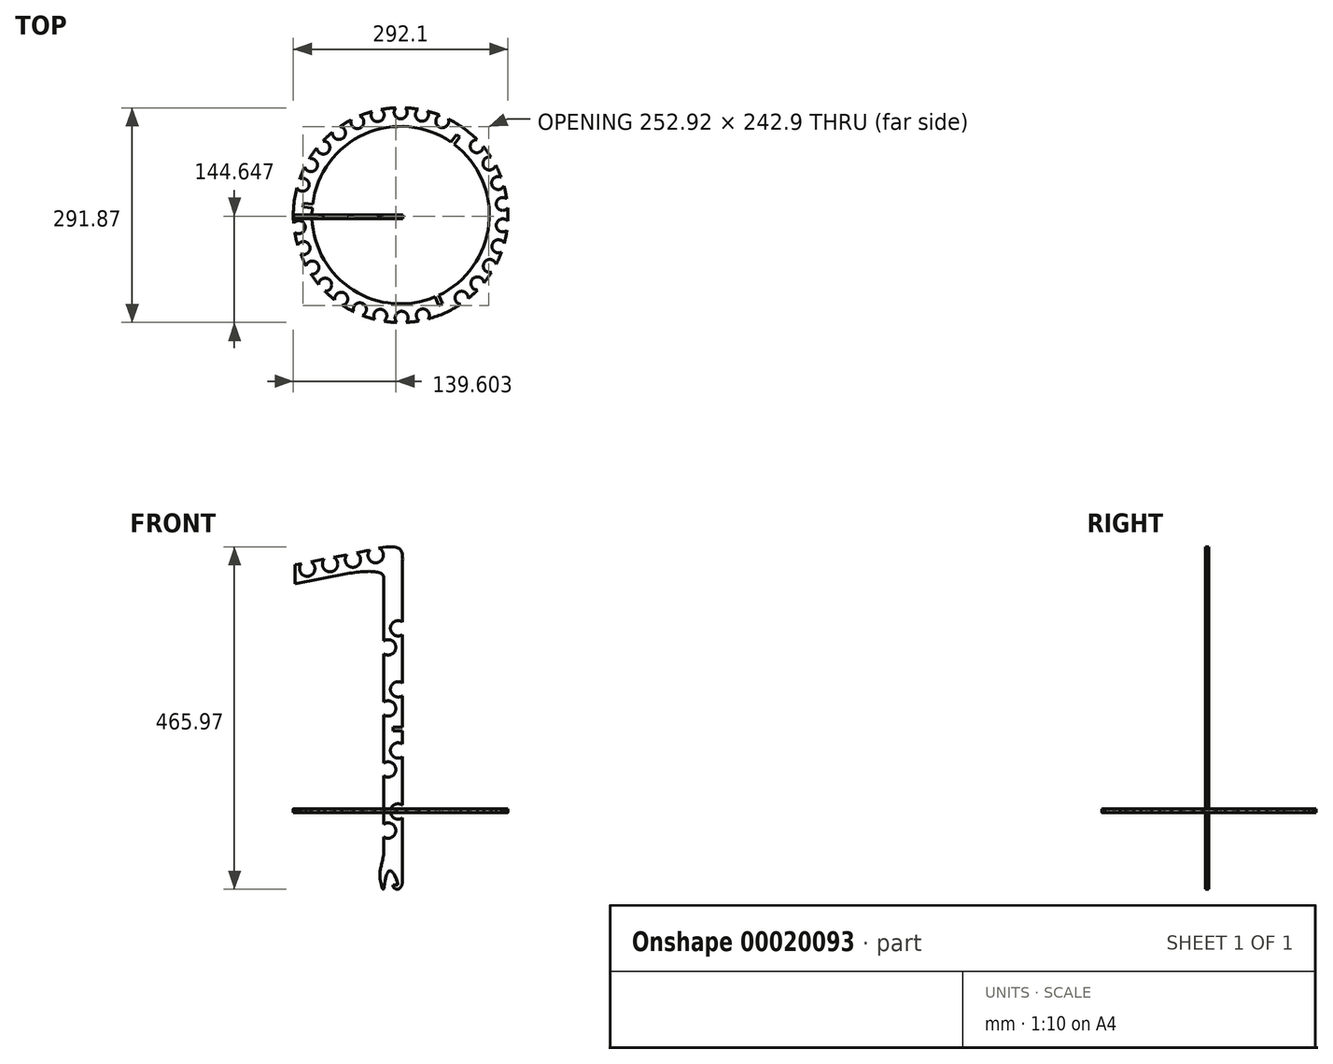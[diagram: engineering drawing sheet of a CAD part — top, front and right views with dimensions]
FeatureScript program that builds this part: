
annotation { "Feature Type Name" : "Feature", "Feature Type Description" : "" }
export const myFeature = defineFeature(function(context is Context, id is Id, definition is map)
    precondition{}
    {
        {
            var Q0;
            Q0=qCreatedBy(makeId("Top.planeOp"),FACE);
            var sketch = newSketch(context, id + "F0", { "sketchPlane" : qUnion([Q0])});
            skArc(sketch, "E0", {"start": v(-6.35, 145.91) * mm, "mid": v(-16.52, 145.11) * mm, "end": v(-26.62, 143.6) * mm});
            skArc(sketch, "E1", {"start": v(-120.25, 9.87) * mm, "mid": v(-70.74, -97.73) * mm, "end": v(46.94, -111.14) * mm});
            skArc(sketch, "E2", {"start": v(-6.35, 145.91) * mm, "mid": v(0, 130.8) * mm, "end": v(6.35, 145.91) * mm});
            skArc(sketch, "E3.1.0", {"start": v(24.04, 144.06) * mm, "mid": v(27.12, 127.96) * mm, "end": v(36.46, 141.42) * mm});
            skArc(sketch, "E3.2.0", {"start": v(53.38, 135.94) * mm, "mid": v(53.06, 119.56) * mm, "end": v(65, 130.8) * mm});
            skArc(sketch, "E3.4.0", {"start": v(103.94, 102.6) * mm, "mid": v(97, 87.75) * mm, "end": v(112.46, 93.18) * mm});
            skArc(sketch, "E3.5.0", {"start": v(122.95, 78.82) * mm, "mid": v(113.08, 65.74) * mm, "end": v(129.34, 67.84) * mm});
            skArc(sketch, "E3.6.0", {"start": v(136.62, 51.62) * mm, "mid": v(124.25, 40.86) * mm, "end": v(140.6, 39.55) * mm});
            skArc(sketch, "E3.7.0", {"start": v(144.36, 22.17) * mm, "mid": v(130.03, 14.22) * mm, "end": v(145.74, 9.55) * mm});
            skArc(sketch, "E3.8.0", {"start": v(145.82, -8.24) * mm, "mid": v(130.15, -13.05) * mm, "end": v(144.55, -20.88) * mm});
            skArc(sketch, "E3.9.0", {"start": v(140.94, -38.3) * mm, "mid": v(124.61, -39.75) * mm, "end": v(137.08, -50.4) * mm});
            skArc(sketch, "E3.10.0", {"start": v(129.94, -66.68) * mm, "mid": v(113.66, -64.72) * mm, "end": v(123.65, -77.72) * mm});
            skArc(sketch, "E3.11.0", {"start": v(113.3, -92.17) * mm, "mid": v(97.78, -86.88) * mm, "end": v(104.85, -101.67) * mm});
            skArc(sketch, "E3.12.0", {"start": v(91.72, -113.66) * mm, "mid": v(77.64, -105.27) * mm, "end": v(81.5, -121.2) * mm});
            skArc(sketch, "E3.14.0", {"start": v(37.73, -141.1) * mm, "mid": v(28.26, -127.71) * mm, "end": v(25.33, -143.84) * mm});
            skArc(sketch, "E3.15.0", {"start": v(7.66, -145.85) * mm, "mid": v(1.17, -130.8) * mm, "end": v(-5.04, -145.96) * mm});
            skArc(sketch, "E3.16.0", {"start": v(-22.75, -144.27) * mm, "mid": v(-25.97, -128.2) * mm, "end": v(-35.2, -141.75) * mm});
            skArc(sketch, "E3.17.0", {"start": v(-52.16, -136.42) * mm, "mid": v(-51.99, -120.03) * mm, "end": v(-63.82, -131.37) * mm});
            skArc(sketch, "E3.18.0", {"start": v(-79.31, -122.64) * mm, "mid": v(-75.74, -106.64) * mm, "end": v(-89.67, -115.28) * mm});
            skArc(sketch, "E3.19.0", {"start": v(-103.02, -103.53) * mm, "mid": v(-96.2, -88.62) * mm, "end": v(-111.62, -94.19) * mm});
            skArc(sketch, "E3.20.0", {"start": v(-122.24, -79.92) * mm, "mid": v(-112.49, -66.75) * mm, "end": v(-128.72, -69) * mm});
            skArc(sketch, "E3.21.0", {"start": v(-136.16, -52.84) * mm, "mid": v(-123.88, -41.98) * mm, "end": v(-140.23, -40.81) * mm});
            skArc(sketch, "E3.22.0", {"start": v(-144.15, -23.46) * mm, "mid": v(-129.9, -15.38) * mm, "end": v(-145.65, -10.85) * mm});
            skArc(sketch, "E3.24.0", {"start": v(-141.28, 37.03) * mm, "mid": v(-124.96, 38.63) * mm, "end": v(-137.53, 49.16) * mm});
            skArc(sketch, "E3.25.0", {"start": v(-130.53, 65.52) * mm, "mid": v(-114.24, 63.7) * mm, "end": v(-124.35, 76.6) * mm});
            skArc(sketch, "E3.26.0", {"start": v(-114.11, 91.15) * mm, "mid": v(-98.55, 86) * mm, "end": v(-105.76, 100.72) * mm});
            skArc(sketch, "E3.27.0", {"start": v(-92.73, 112.83) * mm, "mid": v(-78.58, 104.57) * mm, "end": v(-82.58, 120.46) * mm});
            skArc(sketch, "E3.28.0", {"start": v(-67.33, 129.6) * mm, "mid": v(-55.2, 118.59) * mm, "end": v(-55.81, 134.97) * mm});
            skArc(sketch, "E3.29.0", {"start": v(-39, 140.75) * mm, "mid": v(-29.4, 127.45) * mm, "end": v(-26.62, 143.6) * mm});
            skLineSegment(sketch, "E3.anchor1", {"start": v(0, 0) * mm, "end": v(-6.35, 145.91) * mm, "construction": true});
            skLineSegment(sketch, "E3.anchor2", {"start": v(0, 0) * mm, "end": v(-39, 140.75) * mm, "construction": true});
            skArc(sketch, "E4.trimOffspring", {"start": v(24.04, 144.06) * mm, "mid": v(15.22, 145.25) * mm, "end": v(6.35, 145.91) * mm});
            skLineSegment(sketch, "E5.bottom", {"start": v(76.13, 109.51) * mm, "end": v(80.25, 106.53) * mm});
            skLineSegment(sketch, "E5.left", {"start": v(68.67, 99.2) * mm, "end": v(76.13, 109.51) * mm});
            skLineSegment(sketch, "E5.right", {"start": v(72.78, 96.22) * mm, "end": v(80.25, 106.53) * mm});
            skLineSegment(sketch, "E6", {"start": v(0, 0) * mm, "end": v(81.9, 113.16) * mm, "construction": true});
            skPoint(sketch, "E7", {"position": v(65.28, 90.2) * mm});
            skPoint(sketch, "E8", {"position": v(78.19, 108.02) * mm});
            skLineSegment(sketch, "E9.1.0", {"start": v(-120.25, 9.87) * mm, "end": v(-132.9, 11.17) * mm});
            skLineSegment(sketch, "E9.1.1", {"start": v(-132.9, 11.17) * mm, "end": v(-132.38, 16.23) * mm});
            skLineSegment(sketch, "E9.1.2", {"start": v(-119.72, 14.92) * mm, "end": v(-132.38, 16.23) * mm});
            skLineSegment(sketch, "E9.2.0", {"start": v(51.58, -109.07) * mm, "end": v(56.78, -120.69) * mm});
            skLineSegment(sketch, "E9.2.1", {"start": v(56.78, -120.69) * mm, "end": v(52.14, -122.76) * mm});
            skLineSegment(sketch, "E9.2.2", {"start": v(46.94, -111.14) * mm, "end": v(52.14, -122.76) * mm});
            skArc(sketch, "E10.trimOffspring", {"start": v(53.38, 135.94) * mm, "mid": v(45, 138.94) * mm, "end": v(36.46, 141.42) * mm});
            skArc(sketch, "E11.trimOffspring", {"start": v(103.94, 102.6) * mm, "mid": v(85.63, 118.31) * mm, "end": v(65, 130.8) * mm});
            skArc(sketch, "E12.trimOffspring", {"start": v(122.95, 78.82) * mm, "mid": v(117.93, 86.16) * mm, "end": v(112.46, 93.18) * mm});
            skArc(sketch, "E13.trimOffspring", {"start": v(136.62, 51.62) * mm, "mid": v(133.23, 59.84) * mm, "end": v(129.34, 67.84) * mm});
            skArc(sketch, "E14.trimOffspring", {"start": v(144.36, 22.17) * mm, "mid": v(142.74, 30.92) * mm, "end": v(140.6, 39.55) * mm});
            skArc(sketch, "E15.trimOffspring", {"start": v(145.82, -8.24) * mm, "mid": v(146.05, 0.65) * mm, "end": v(145.74, 9.55) * mm});
            skArc(sketch, "E16.trimOffspring", {"start": v(-39, 140.75) * mm, "mid": v(-47.49, 138.11) * mm, "end": v(-55.81, 134.97) * mm});
            skArc(sketch, "E17.trimOffspring", {"start": v(-67.33, 129.6) * mm, "mid": v(-75.1, 125.27) * mm, "end": v(-82.58, 120.46) * mm});
            skArc(sketch, "E18.trimOffspring", {"start": v(-92.73, 112.83) * mm, "mid": v(-99.43, 106.98) * mm, "end": v(-105.76, 100.72) * mm});
            skArc(sketch, "E19.trimOffspring", {"start": v(-114.11, 91.15) * mm, "mid": v(-119.45, 84.04) * mm, "end": v(-124.35, 76.6) * mm});
            skArc(sketch, "E20.trimOffspring", {"start": v(-130.53, 65.52) * mm, "mid": v(-134.28, 57.45) * mm, "end": v(-137.53, 49.16) * mm});
            skArc(sketch, "E21.trimOffspring", {"start": v(-141.28, 37.03) * mm, "mid": v(-145.45, 13.27) * mm, "end": v(-145.65, -10.85) * mm});
            skPoint(sketch, "E22.orphan", {"position": v(-144.73, 19.58) * mm});
            skPoint(sketch, "E23.orphan", {"position": v(-145.89, 6.93) * mm});
            skPoint(sketch, "E24.orphan", {"position": v(-111.01, 8.91) * mm});
            skArc(sketch, "E25.trimOffspring", {"start": v(-144.15, -23.46) * mm, "mid": v(-142.46, -32.2) * mm, "end": v(-140.23, -40.81) * mm});
            skArc(sketch, "E26.trimOffspring", {"start": v(-136.16, -52.84) * mm, "mid": v(-132.69, -61.03) * mm, "end": v(-128.72, -69) * mm});
            skArc(sketch, "E27.trimOffspring", {"start": v(-122.24, -79.92) * mm, "mid": v(-117.15, -87.22) * mm, "end": v(-111.62, -94.19) * mm});
            skArc(sketch, "E28.trimOffspring", {"start": v(-103.02, -103.53) * mm, "mid": v(-96.52, -109.6) * mm, "end": v(-89.67, -115.28) * mm});
            skArc(sketch, "E29.trimOffspring", {"start": v(-79.31, -122.64) * mm, "mid": v(-71.7, -127.24) * mm, "end": v(-63.82, -131.37) * mm});
            skArc(sketch, "E30.trimOffspring", {"start": v(-52.16, -136.42) * mm, "mid": v(-43.76, -139.34) * mm, "end": v(-35.2, -141.75) * mm});
            skArc(sketch, "E31.trimOffspring", {"start": v(-22.75, -144.27) * mm, "mid": v(-13.92, -145.39) * mm, "end": v(-5.04, -145.96) * mm});
            skArc(sketch, "E32.trimOffspring", {"start": v(7.66, -145.85) * mm, "mid": v(16.52, -145.11) * mm, "end": v(25.33, -143.84) * mm});
            skArc(sketch, "E33.trimOffspring", {"start": v(37.73, -141.1) * mm, "mid": v(60.44, -132.96) * mm, "end": v(81.5, -121.2) * mm});
            skPoint(sketch, "E34.orphan", {"position": v(54.6, -135.46) * mm});
            skPoint(sketch, "E35.orphan", {"position": v(66.16, -130.2) * mm});
            skPoint(sketch, "E36.orphan", {"position": v(47.79, -100.6) * mm});
            skPoint(sketch, "E37.orphan", {"position": v(43.15, -102.67) * mm});
            skArc(sketch, "E38.trimOffspring", {"start": v(51.58, -109.07) * mm, "mid": v(120.01, -12.4) * mm, "end": v(72.78, 96.22) * mm});
            skArc(sketch, "E39.trimOffspring", {"start": v(91.72, -113.66) * mm, "mid": v(98.47, -107.86) * mm, "end": v(104.85, -101.67) * mm});
            skArc(sketch, "E40.trimOffspring", {"start": v(113.3, -92.17) * mm, "mid": v(118.7, -85.1) * mm, "end": v(123.65, -77.72) * mm});
            skArc(sketch, "E41.trimOffspring", {"start": v(129.94, -66.68) * mm, "mid": v(133.76, -58.65) * mm, "end": v(137.08, -50.4) * mm});
            skArc(sketch, "E42.trimOffspring", {"start": v(140.94, -38.3) * mm, "mid": v(143.01, -29.64) * mm, "end": v(144.55, -20.88) * mm});
            skPoint(sketch, "E43.orphan", {"position": v(80.4, 121.92) * mm});
            skPoint(sketch, "E44.orphan", {"position": v(90.7, 114.48) * mm});
            skArc(sketch, "E45.trimOffspring", {"start": v(68.67, 99.2) * mm, "mid": v(-49.27, 110.13) * mm, "end": v(-119.72, 14.92) * mm});
            skPoint(sketch, "E46.orphan", {"position": v(63.23, 91.68) * mm});
            skPoint(sketch, "E47.orphan", {"position": v(67.34, 88.7) * mm});
            skSolve(sketch);
        }
        {
            var Q0;
            Q0=qCreatedBy(makeId("Front.planeOp"),FACE);
            var sketch = newSketch(context, id + "F1", { "sketchPlane" : qUnion([Q0])});
            skLineSegment(sketch, "E48.right", {"start": v(2.52, 336.76) * mm, "end": v(2.52, 258.91) * mm});
            skLineSegment(sketch, "E49", {"start": v(2.52, -101.27) * mm, "end": v(-53.55, -101.27) * mm, "construction": true});
            skLineSegment(sketch, "E50", {"start": v(-53.92, -98.73) * mm, "end": v(32.34, -98.73) * mm, "construction": true});
            skLineSegment(sketch, "E51", {"start": v(-64.1, -82.22) * mm, "end": v(32.74, -82.22) * mm, "construction": true});
            skLineSegment(sketch, "E52", {"start": v(-22.25, -118.82) * mm, "end": v(-22.25, -51.09) * mm, "construction": true});
            skLineSegment(sketch, "E53", {"start": v(-3.83, -118.12) * mm, "end": v(-3.83, -101.27) * mm, "construction": true});
            skFitSpline(sketch, "E54", {"points": [v(-3.83, -98.73) * mm, v(-22.25, -101.27) * mm], "startDerivative": vector(-9.39, 49.53) * mm, "endDerivative": vector(-9.44, -109.81) * mm});
            skLineSegment(sketch, "E55", {"start": v(-3.83, -98.73) * mm, "end": v(-10.18, -98.73) * mm});
            skLineSegment(sketch, "E56", {"start": v(-10.18, -98.73) * mm, "end": v(-10.18, -101.27) * mm});
            skFitSpline(sketch, "E57", {"points": [v(-22.88, -49.2) * mm, v(-25.52, -101.27) * mm], "startDerivative": vector(0, -71.49) * mm, "endDerivative": vector(22.98, -71.23) * mm});
            skArc(sketch, "E58", {"start": v(-10.18, -101.27) * mm, "mid": v(-7.51, -103.76) * mm, "end": v(-3.98, -104.72) * mm});
            skFitSpline(sketch, "E59", {"points": [v(2.52, -90.63) * mm, v(-3.98, -104.72) * mm], "startDerivative": vector(0, -24.31) * mm, "endDerivative": vector(-14.9, -5.18) * mm});
            skLineSegment(sketch, "E60.trimOffspring", {"start": v(2.52, -98.73) * mm, "end": v(2.52, -98.74) * mm});
            skFitSpline(sketch, "E61", {"points": [v(-25.52, -101.27) * mm, v(-22.25, -101.27) * mm], "startDerivative": vector(1.55, -13.63) * mm, "endDerivative": vector(0, 10.4) * mm});
            skLineSegment(sketch, "E62.trimOffspring", {"start": v(-22.88, 196.92) * mm, "end": v(-22.88, 150.1) * mm});
            skArc(sketch, "E63", {"start": v(-22.88, -33.48) * mm, "mid": v(-6.64, -24.73) * mm, "end": v(-22.88, -15.98) * mm});
            skArc(sketch, "E64", {"start": v(2.52, 9.77) * mm, "mid": v(-13.92, 1.15) * mm, "end": v(2.52, -7.47) * mm});
            skArc(sketch, "E65.0.1.0", {"start": v(2.52, 92.82) * mm, "mid": v(-13.92, 84.2) * mm, "end": v(2.52, 75.58) * mm});
            skArc(sketch, "E65.0.1.1", {"start": v(-22.88, 49.57) * mm, "mid": v(-6.64, 58.32) * mm, "end": v(-22.88, 67.06) * mm});
            skArc(sketch, "E65.0.2.0", {"start": v(2.52, 175.87) * mm, "mid": v(-13.92, 167.25) * mm, "end": v(2.52, 158.63) * mm});
            skArc(sketch, "E65.0.2.1", {"start": v(-22.88, 132.61) * mm, "mid": v(-6.64, 141.36) * mm, "end": v(-22.88, 150.1) * mm});
            skArc(sketch, "E65.0.3.0", {"start": v(2.52, 258.91) * mm, "mid": v(-13.92, 250.3) * mm, "end": v(2.52, 241.67) * mm});
            skArc(sketch, "E65.0.3.1", {"start": v(-22.88, 215.66) * mm, "mid": v(-6.64, 224.4) * mm, "end": v(-22.88, 233.15) * mm});
            skLineSegment(sketch, "E65.direction1", {"start": v(-3.44, 1.15) * mm, "end": v(18.1, 1.15) * mm, "construction": true});
            skLineSegment(sketch, "E65.direction2", {"start": v(-3.44, 1.15) * mm, "end": v(-3.44, 84.2) * mm, "construction": true});
            skLineSegment(sketch, "E66.trimOffspring", {"start": v(2.52, -7.47) * mm, "end": v(2.52, -90.63) * mm});
            skLineSegment(sketch, "E67.trimOffspring", {"start": v(-22.88, -33.48) * mm, "end": v(-22.88, -49.2) * mm});
            skLineSegment(sketch, "E68.trimOffspring", {"start": v(-22.88, 49.57) * mm, "end": v(-22.88, -15.98) * mm});
            skLineSegment(sketch, "E69.trimOffspring", {"start": v(2.52, 75.58) * mm, "end": v(2.52, 9.77) * mm});
            skLineSegment(sketch, "E70.trimOffspring", {"start": v(-22.88, 132.61) * mm, "end": v(-22.88, 67.06) * mm});
            skLineSegment(sketch, "E71.trimOffspring", {"start": v(2.52, 158.63) * mm, "end": v(2.52, 115.9) * mm});
            skLineSegment(sketch, "E72.trimOffspring", {"start": v(2.52, 241.67) * mm, "end": v(2.52, 175.87) * mm});
            skLineSegment(sketch, "E73.trimOffspring", {"start": v(-22.88, 215.66) * mm, "end": v(-22.88, 202) * mm});
            skLineSegment(sketch, "E74", {"start": v(-22.88, 202) * mm, "end": v(-22.88, 196.92) * mm});
            skLineSegment(sketch, "E75.bottom", {"start": v(2.52, 115.9) * mm, "end": v(-10.18, 115.9) * mm});
            skLineSegment(sketch, "E75.top", {"start": v(2.52, 110.82) * mm, "end": v(-10.18, 110.82) * mm});
            skLineSegment(sketch, "E75.right", {"start": v(-10.18, 115.9) * mm, "end": v(-10.18, 110.82) * mm});
            skLineSegment(sketch, "E76.top", {"start": v(-72.33, 324.73) * mm, "end": v(-143.53, 310.72) * mm});
            skLineSegment(sketch, "E76.right", {"start": v(-143.53, 336.03) * mm, "end": v(-143.53, 310.72) * mm});
            skFitSpline(sketch, "E77", {"points": [v(-46.67, 355.67) * mm, v(2.52, 336.76) * mm], "startDerivative": vector(162.8, 41.86) * mm, "endDerivative": vector(0, -55.35) * mm});
            skLineSegment(sketch, "E78.trimOffspring", {"start": v(-22.88, 319.01) * mm, "end": v(-22.88, 233.15) * mm});
            skFitSpline(sketch, "E79", {"points": [v(-72.33, 324.73) * mm, v(-22.88, 319.01) * mm], "startDerivative": vector(70.9, 11.87) * mm, "endDerivative": vector(0, -33.73) * mm});
            skLineSegment(sketch, "E80", {"start": v(-127.14, 331.49) * mm, "end": v(-36.29, 349.36) * mm, "construction": true});
            skLineSegment(sketch, "E81.trimOffspring", {"start": v(-116.28, 341.97) * mm, "end": v(-122.31, 340.79) * mm});
            skLineSegment(sketch, "E82", {"start": v(-28.38, 359.72) * mm, "end": v(-29.81, 359.4) * mm});
            skLineSegment(sketch, "E83", {"start": v(-116.28, 341.97) * mm, "end": v(-104.06, 344.38) * mm});
            skLineSegment(sketch, "E84", {"start": v(-143.53, 336.61) * mm, "end": v(-143.53, 336.03) * mm});
            skArc(sketch, "E85", {"start": v(-135.13, 338.26) * mm, "mid": v(-125.12, 321.2) * mm, "end": v(-122.31, 340.79) * mm});
            skArc(sketch, "E86.1.0.0", {"start": v(-104.06, 344.38) * mm, "mid": v(-94.06, 327.3) * mm, "end": v(-91.27, 346.9) * mm});
            skArc(sketch, "E86.2.0.0", {"start": v(-72.99, 350.49) * mm, "mid": v(-63, 333.4) * mm, "end": v(-60.22, 353) * mm});
            skArc(sketch, "E86.3.0.0", {"start": v(-41.78, 356.75) * mm, "mid": v(-31.7, 339.55) * mm, "end": v(-29.81, 359.4) * mm});
            skLineSegment(sketch, "E86.direction1", {"start": v(-127.14, 331.49) * mm, "end": v(-96.08, 337.59) * mm, "construction": true});
            skLineSegment(sketch, "E87.trimOffspring", {"start": v(-135.13, 338.26) * mm, "end": v(-143.53, 336.61) * mm});
            skLineSegment(sketch, "E88.trimOffspring", {"start": v(-91.27, 346.9) * mm, "end": v(-72.99, 350.49) * mm});
            skLineSegment(sketch, "E89.trimOffspring", {"start": v(-60.22, 353) * mm, "end": v(-46.67, 355.67) * mm});
            skLineSegment(sketch, "E90.trimOffspring", {"start": v(-41.78, 356.75) * mm, "end": v(-46.67, 355.67) * mm});
            skLineSegment(sketch, "E91.trimOffspring", {"start": v(2.52, 110.82) * mm, "end": v(2.52, 92.82) * mm});
            skPoint(sketch, "E48.top.end.orphan", {"position": v(-3.83, -101.27) * mm});
            skLineSegment(sketch, "E92.trimOffspring", {"start": v(-3.83, -98.73) * mm, "end": v(-3.83, -51.09) * mm, "construction": true});
            skSolve(sketch);
        }
        {
            var Q0;
            Q0=makeQuery(id+"F1.imprint","IMPRINT",FACE,{"disambiguationData":[TD([[makeQuery(id+"F1.imprint","IMPRINT",EDGE,{"derivedFrom":sQuery(id+"F1.wireOp",EDGE,"E48.right")}),-1.0]])]});
            extrude(context, id + "F2", {"entities" : qUnion([Q0]), "depth" : 5.08 * mm});
        }
        {
            var Q0;
            Q0=makeQuery(id+"F0.imprint","IMPRINT",FACE,{"disambiguationData":[TD([[makeQuery(id+"F0.imprint","IMPRINT",EDGE,{"derivedFrom":sQuery(id+"F0.wireOp",EDGE,"E0")}),1.0]])]});
            extrude(context, id + "F3", {"entities" : qUnion([Q0]), "depth" : 5.08 * mm});
        }
    });
